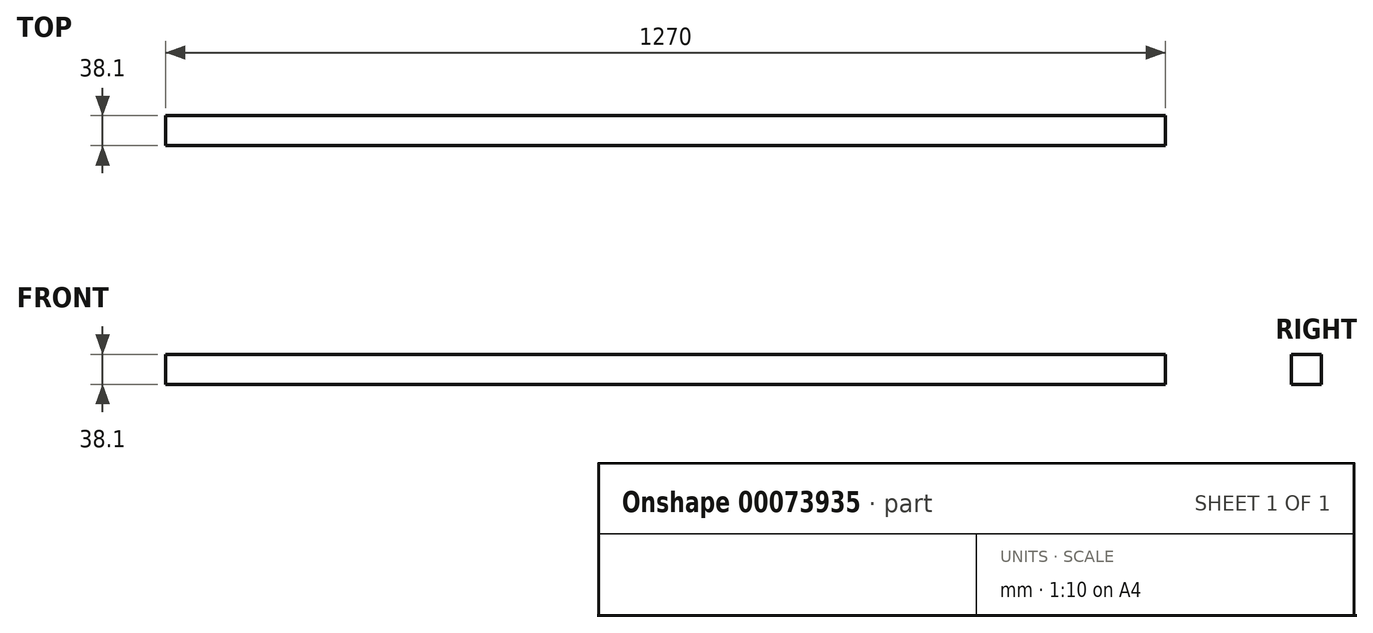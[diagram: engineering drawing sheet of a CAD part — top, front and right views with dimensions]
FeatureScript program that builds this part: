
annotation { "Feature Type Name" : "Feature", "Feature Type Description" : "" }
export const myFeature = defineFeature(function(context is Context, id is Id, definition is map)
    precondition{}
    {
        {
            var Q0;
            Q0=qCreatedBy(makeId("Front.planeOp"),FACE);
            var sketch = newSketch(context, id + "F0", { "sketchPlane" : qUnion([Q0])});
            skLineSegment(sketch, "E0.rect.bottom", {"start": v(-635, 19.05) * mm, "end": v(635, 19.05) * mm});
            skLineSegment(sketch, "E0.rect.top", {"start": v(-635, -19.05) * mm, "end": v(635, -19.05) * mm});
            skLineSegment(sketch, "E0.rect.left", {"start": v(-635, 19.05) * mm, "end": v(-635, -19.05) * mm});
            skLineSegment(sketch, "E0.rect.right", {"start": v(635, 19.05) * mm, "end": v(635, -19.05) * mm});
            skPoint(sketch, "E0.rect.middle", {"position": v(0, 0) * mm});
            skSolve(sketch);
        }
        {
            var Q0;
            Q0 = qSketchRegion(id + "F0", true);
            extrude(context, id + "F1", {"entities" : qUnion([Q0]), "endBound" : BoundingType.SYMMETRIC, "depth" : 38.1 * mm});
        }
    });
